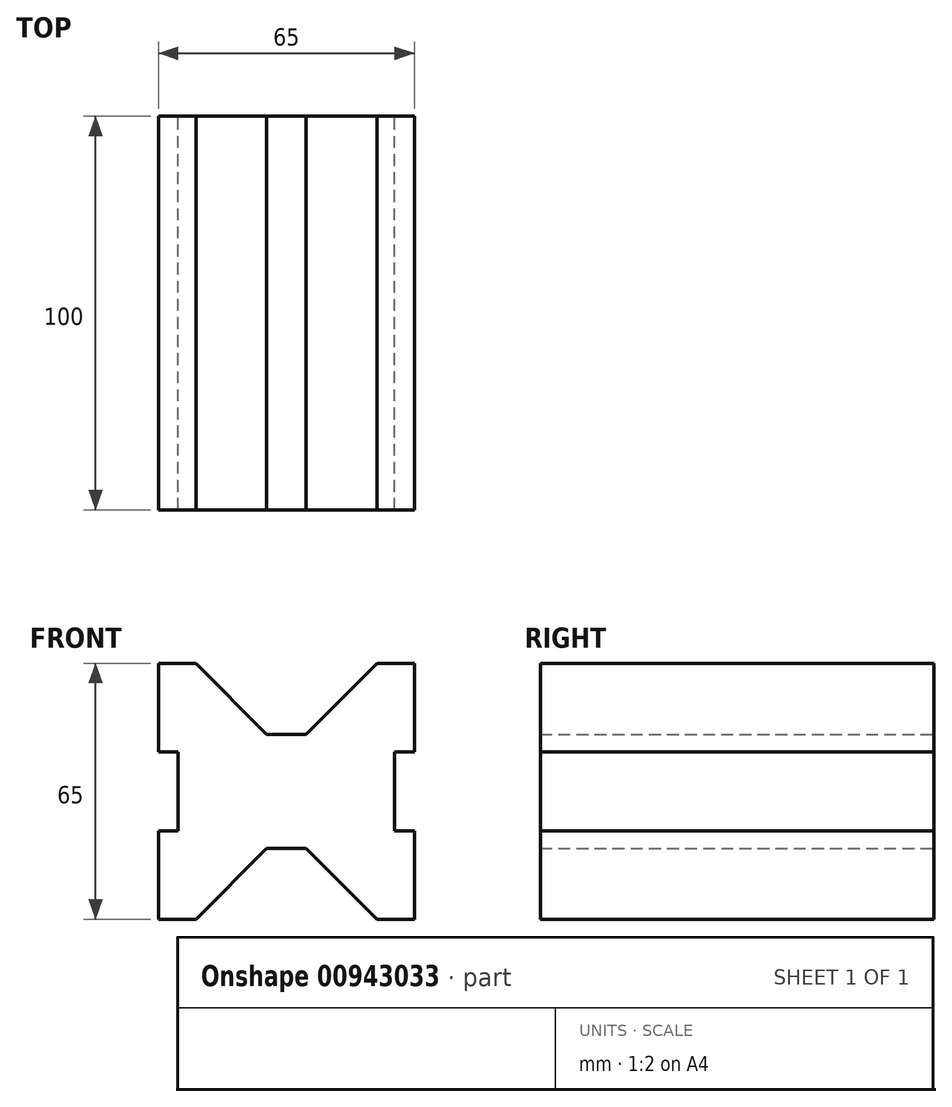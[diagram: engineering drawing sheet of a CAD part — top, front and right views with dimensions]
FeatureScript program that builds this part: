
annotation { "Feature Type Name" : "Feature", "Feature Type Description" : "" }
export const myFeature = defineFeature(function(context is Context, id is Id, definition is map)
    precondition{}
    {
        {
            var Q0;
            Q0=qCreatedBy(makeId("Front.planeOp"),FACE);
            var sketch = newSketch(context, id + "F0", { "sketchPlane" : qUnion([Q0])});
            skLineSegment(sketch, "E0", {"start": v(0, 42.8) * mm, "end": v(0, -43.08) * mm, "construction": true});
            skLineSegment(sketch, "E1", {"start": v(0, 14.5) * mm, "end": v(-5, 14.5) * mm});
            skLineSegment(sketch, "E2", {"start": v(-5, 14.5) * mm, "end": v(-23, 32.5) * mm});
            skLineSegment(sketch, "E3", {"start": v(-23, 32.5) * mm, "end": v(-32.5, 32.5) * mm});
            skLineSegment(sketch, "E4", {"start": v(-32.5, 32.5) * mm, "end": v(-32.5, 10) * mm});
            skLineSegment(sketch, "E5", {"start": v(-32.5, 10) * mm, "end": v(-27.5, 10) * mm});
            skLineSegment(sketch, "E6", {"start": v(-27.5, 10) * mm, "end": v(-27.5, -10) * mm});
            skLineSegment(sketch, "E7", {"start": v(-27.5, -10) * mm, "end": v(-32.5, -10) * mm});
            skLineSegment(sketch, "E8", {"start": v(-32.5, -10) * mm, "end": v(-32.5, -32.5) * mm});
            skLineSegment(sketch, "E9", {"start": v(-32.5, -32.5) * mm, "end": v(-23, -32.5) * mm});
            skLineSegment(sketch, "E10", {"start": v(-5, -14.5) * mm, "end": v(-23, -32.5) * mm});
            skLineSegment(sketch, "E11", {"start": v(-5, -14.5) * mm, "end": v(0, -14.5) * mm});
            skLineSegment(sketch, "E12", {"start": v(0, -14.5) * mm, "end": v(0, 14.5) * mm});
            skLineSegment(sketch, "E13.MirrorCS", {"start": v(0, 14.5) * mm, "end": v(5, 14.5) * mm});
            skLineSegment(sketch, "E14.MirrorCS", {"start": v(5, 14.5) * mm, "end": v(23, 32.5) * mm});
            skLineSegment(sketch, "E15.MirrorCS", {"start": v(23, 32.5) * mm, "end": v(32.5, 32.5) * mm});
            skLineSegment(sketch, "E16.MirrorCS", {"start": v(32.5, 32.5) * mm, "end": v(32.5, 10) * mm});
            skLineSegment(sketch, "E17.MirrorCS", {"start": v(32.5, 10) * mm, "end": v(27.5, 10) * mm});
            skLineSegment(sketch, "E18.MirrorCS", {"start": v(27.5, 10) * mm, "end": v(27.5, -10) * mm});
            skLineSegment(sketch, "E19.MirrorCS", {"start": v(27.5, -10) * mm, "end": v(32.5, -10) * mm});
            skLineSegment(sketch, "E20.MirrorCS", {"start": v(32.5, -10) * mm, "end": v(32.5, -32.5) * mm});
            skLineSegment(sketch, "E21.MirrorCS", {"start": v(32.5, -32.5) * mm, "end": v(23, -32.5) * mm});
            skLineSegment(sketch, "E22.MirrorCS", {"start": v(5, -14.5) * mm, "end": v(23, -32.5) * mm});
            skLineSegment(sketch, "E23.MirrorCS", {"start": v(5, -14.5) * mm, "end": v(0, -14.5) * mm});
            skSolve(sketch);
        }
        {
            var Q0;
            Q0=qSketchRegion(id+"F0",true);
            extrude(context, id + "F1", {"entities" : qUnion([Q0]), "depth" : 100 * mm, "offsetDistance" : 25 * mm, "symmetric" : true});
        }
    });
